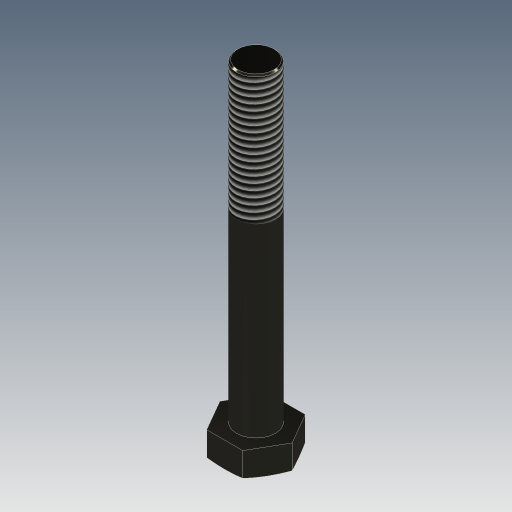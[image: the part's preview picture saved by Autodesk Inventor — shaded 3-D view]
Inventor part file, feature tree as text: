
AUTODESK INVENTOR PART (.ipt)
format: ipt  version: 2023.1 (Build 271208000, 208)  size: 149,504 bytes
history: native  units: mm
features: sketch x3, revolve x2, thread x1, extrude x1
ambient origin geometry x8: Origin, YZ Plane, XZ Plane, XY Plane, X Axis, Y Axis, Z Axis, Center Point
bodies: Solido1 (feature_tree)
feature tree (7):
  revolve  "Rivoluzione1"
  thread  "Filettatura1"
  extrude  "Estrusione1"  Depth=5.2mm
  revolve  "Rivoluzione3"
  sketch  "Schizzo4"
  sketch  "Schizzo5"
  sketch  "Schizzo6"
